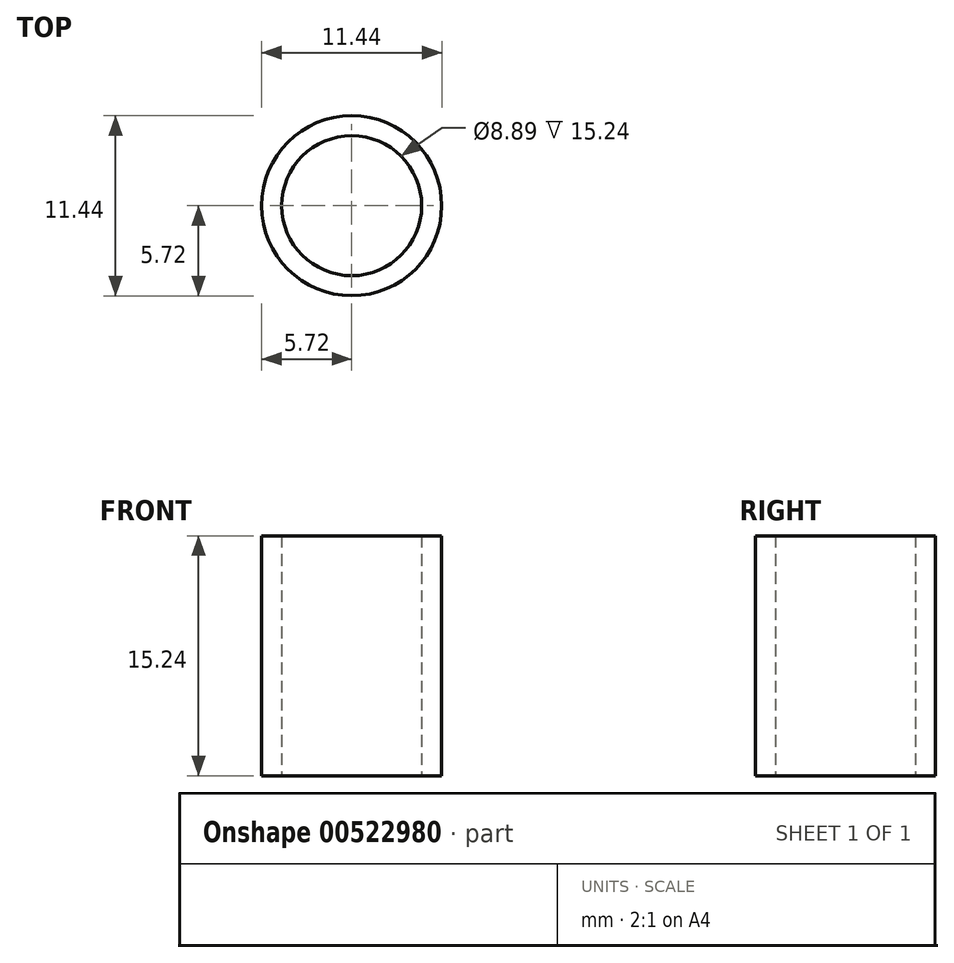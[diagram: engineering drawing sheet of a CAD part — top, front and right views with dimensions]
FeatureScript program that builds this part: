
annotation { "Feature Type Name" : "Feature", "Feature Type Description" : "" }
export const myFeature = defineFeature(function(context is Context, id is Id, definition is map)
    precondition{}
    {
        {
            var Q0;
            Q0=qCreatedBy(makeId("Top.planeOp"),FACE);
            var sketch = newSketch(context, id + "F0", { "sketchPlane" : qUnion([Q0])});
            skCircle(sketch, "E0", {"center": v(0, 0) * mm, "radius": 5.72 * mm});
            skCircle(sketch, "E1", {"center": v(0, 0) * mm, "radius": 4.45 * mm});
            skSolve(sketch);
        }
        {
            var Q0;
            Q0 = qSketchRegion(id + "F0", true);
            extrude(context, id + "F1", {"entities" : qUnion([Q0]), "depth" : 15.24 * mm, "offsetDistance" : 25.4 * mm});
        }
    });
